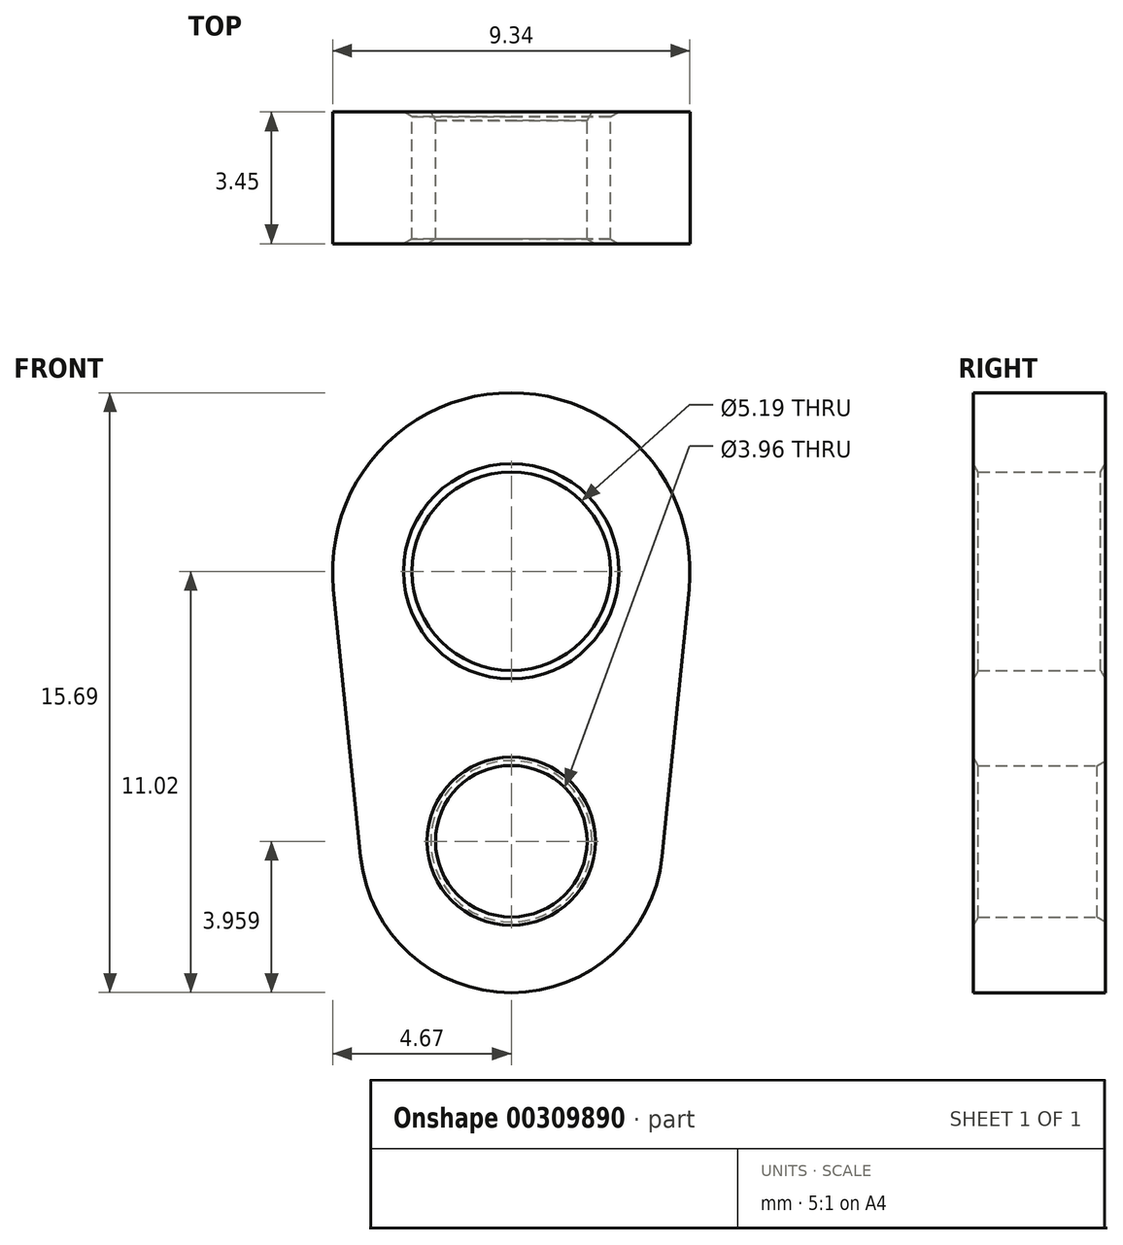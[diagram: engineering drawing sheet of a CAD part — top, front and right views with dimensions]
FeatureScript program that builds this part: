
annotation { "Feature Type Name" : "Feature", "Feature Type Description" : "" }
export const myFeature = defineFeature(function(context is Context, id is Id, definition is map)
    precondition{}
    {
        {
            var Q0;
            Q0=qCreatedBy(makeId("Front.planeOp"),FACE);
            var sketch = newSketch(context, id + "F0", { "sketchPlane" : qUnion([Q0])});
            skCircle(sketch, "E0", {"center": v(0, 0) * mm, "radius": 2.6 * mm});
            skCircle(sketch, "E1", {"center": v(0, -7.06) * mm, "radius": 1.98 * mm});
            skArc(sketch, "E2", {"start": v(-3.94, -7.46) * mm, "mid": v(0, -11.02) * mm, "end": v(3.94, -7.46) * mm});
            skArc(sketch, "E3", {"start": v(4.65, -0.47) * mm, "mid": v(0, 4.67) * mm, "end": v(-4.65, -0.47) * mm});
            skLineSegment(sketch, "E4", {"start": v(-3.94, -7.46) * mm, "end": v(-4.65, -0.47) * mm});
            skLineSegment(sketch, "E5", {"start": v(3.94, -7.46) * mm, "end": v(4.65, -0.47) * mm});
            skSolve(sketch);
        }
        {
            var Q0;
            Q0=makeQuery(id+"F0.imprint","IMPRINT",FACE,{"disambiguationData":[TD([[makeQuery(id+"F0.imprint","IMPRINT",EDGE,{"derivedFrom":sQuery(id+"F0.wireOp",EDGE,"E0")}),-1.0]])]});
            extrude(context, id + "F1", {"entities" : qUnion([Q0]), "depth" : 3.45 * mm});
        }
        {
            var Q0;
            Q0=makeQuery(id+"F1.opExtrude","CAP_EDGE",EDGE,{"disambiguationData":[OSD([sQuery(id+"F0.wireOp",EDGE,"E0")])],"isStart":false});
            var Q1;
            Q1=makeQuery(id+"F1.opExtrude","CAP_EDGE",EDGE,{"disambiguationData":[OSD([sQuery(id+"F0.wireOp",EDGE,"E1")])],"isStart":false});
            var Q2;
            Q2=makeQuery(id+"F1.opExtrude","CAP_EDGE",EDGE,{"disambiguationData":[OSD([sQuery(id+"F0.wireOp",EDGE,"E0")])],"isStart":true});
            var Q3;
            Q3=makeQuery(id+"F1.opExtrude","CAP_EDGE",EDGE,{"disambiguationData":[OSD([sQuery(id+"F0.wireOp",EDGE,"E1")])],"isStart":true});
            chamfer(context, id + "F2", {"entities" : qUnion([Q0, Q1, Q2, Q3]), "chamferType" : ChamferType.OFFSET_ANGLE, "width" : 0.13 * mm, "oppositeDirection" : false, "angle" : 60 * degree, "tangentPropagation" : true});
        }
    });
